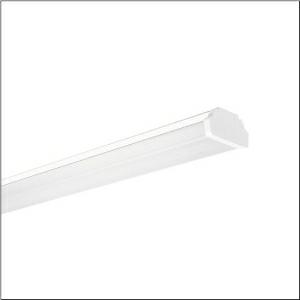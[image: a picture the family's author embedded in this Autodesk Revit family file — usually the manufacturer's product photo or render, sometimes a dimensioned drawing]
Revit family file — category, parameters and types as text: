
# Revit family: dus_31_gen_2_53bd812mv485c2_9aef
name_source: partatom
category: Lighting Fixtures
units: mm (PartAtom-declared; Revit-internal decimal feet)

## family parameters
Cut with Voids When Loaded = No
Host = Face
Light Source = No
Part Type = Normal
Room Calculation Point = No
Round Connector Dimension = Use Diameter
Shared = No

## types (1)
- --- (1 x LED, 8950 lm, 48.2 W, 4000K)
    Apparent Load = 48 VA
    CIE Flux Codes = 47 80 95 93 100
    Color Rendering = 80
    Color Temperature = 4000K
    Default Elevation = 1800 mm
    Description = DUS 31 Gen.2, luminaire insert, of sheet steel, coil coated, white, length: 1.535mm, width: 81mm, height: 90mm, 5x system unit, system units: 307mm, LED rated luminous flux: 8.950lm, light colour: 840, SDCM (Standard Deviation of Colour Matching)MacAdam ≤ 3 SDCM (initial), control gear: ON/OFF Multilumen, control gear: ECG, with plug, 3-pole, with phase selection, mains connection: 220..240V, AC, 50/60Hz, rated input power: 48W, through-wiring accessed according to module size, primary optical cover: cover, of PMMA, light emission: direct distribution, primary light characteristic: symmetric, protection rating (complete): IP20, protection rating (LED compartment): IP50, insulation class (complete): insulation class I (protective earthing), certification: CE, ENEC, VDE, UKCA, impact resistance: IK03, permissible ambient temperature for indoor applications: -35..+50°C, corresponds to IFS (International Featured Standards) requirements for safety and quality in the food industry, reducing of maximum allowable ambient temperature of 5°C with ceiling mounting, packaging unit: 1 piece
    Height = 95 mm
    Lamp = 1 x LED
    Lamp Light Flux = 8950 lm
    Lamp Power = 48.2 W
    Lamp count = 1
    Length = 1535 mm
    Luminous efficacy = 186 lm/W
    Manufacturer = Siteco
    ModVariant = No
    Model = 53BD812MV485C2
    Mounting Place = Ceiling
    Mounting Type = Pendant
    Number of Poles = 1
    OnlyDefault = Yes
    Power Factor = 1
    Product Name = DUS 31 Gen.2
    Product group = luminaire insert | ceiling pendant
    ProductGroupID = 901
    Protection Class = Protection class I
    Protection Degree = IP 20
    RLX_Detail_Level = 1
    RLX_Emergency_Light_Flux = 0 lm
    RLX_Emergency_Type = 0
    RLX_Emergency_Type_DB = No
    RlxData = <blob elided: 29833 chars, md5=e821f574>
    Socket = socket
    Standby Power = 0 W
    System Light Flux = 8950 lm
    System Power = 48 W
    Type Comments = factory setting: luminous flux: 100 % | (A | C | E) | 112 mA
    Type Image = l_1319596.jpg
    URL = http://relux.com
    VarID = @adj_040851
    Voltage = 0 V
    Weight = 0.00 kg
    Width = 81 mm

## geometry (parser evidence)
native form markers: Blend x4, Sweep x12
no freeform markers — native parametric forms only
